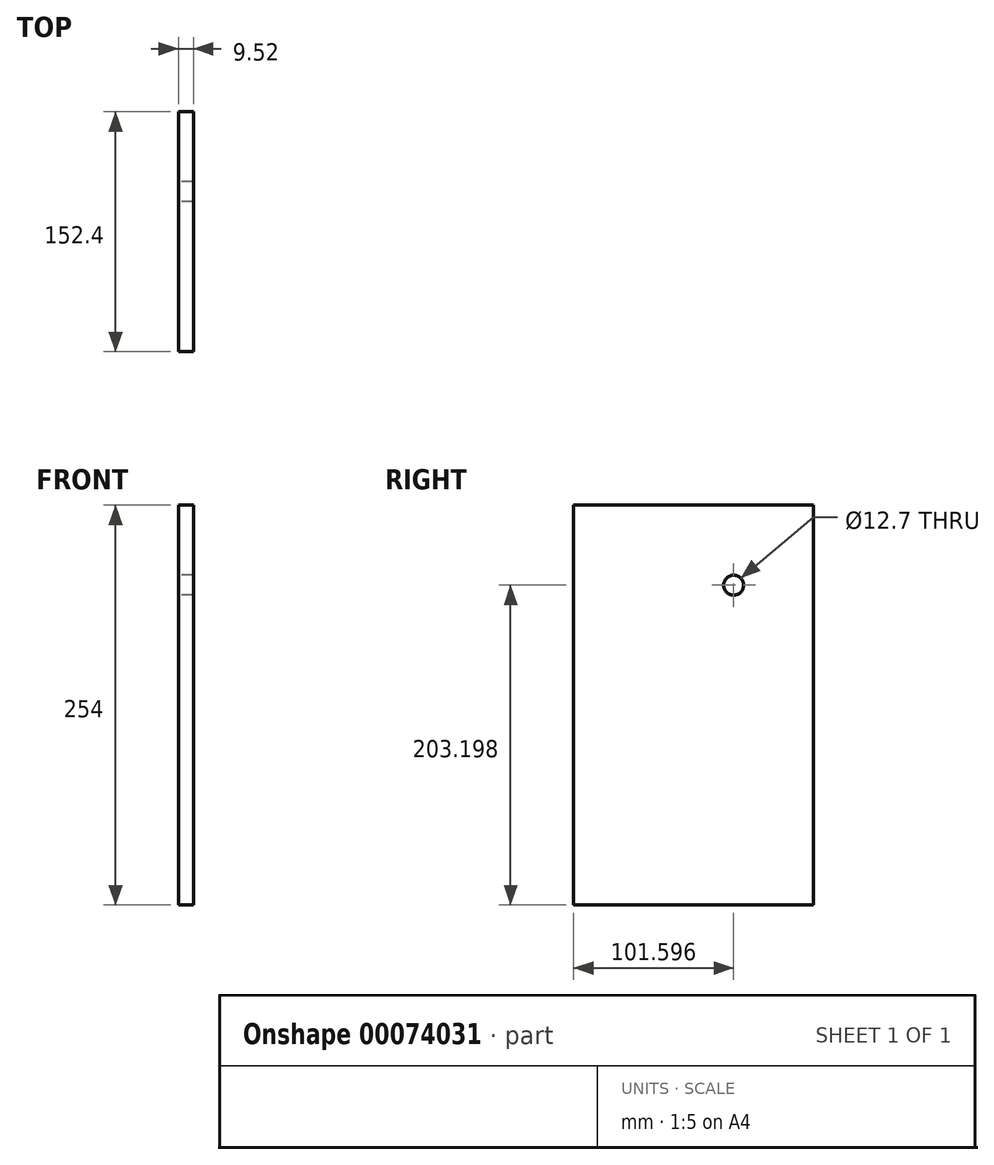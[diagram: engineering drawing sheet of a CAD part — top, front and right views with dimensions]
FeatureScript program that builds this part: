
annotation { "Feature Type Name" : "Feature", "Feature Type Description" : "" }
export const myFeature = defineFeature(function(context is Context, id is Id, definition is map)
    precondition{}
    {
        {
            var Q0;
            Q0=qCreatedBy(makeId("Right.planeOp"),FACE);
            var sketch = newSketch(context, id + "F0", { "sketchPlane" : qUnion([Q0])});
            skLineSegment(sketch, "E0.bottom", {"start": v(-96.53, 165.43) * mm, "end": v(55.87, 165.43) * mm});
            skLineSegment(sketch, "E0.top", {"start": v(-96.53, -88.57) * mm, "end": v(55.87, -88.57) * mm});
            skLineSegment(sketch, "E0.left", {"start": v(-96.53, 165.43) * mm, "end": v(-96.53, -88.57) * mm});
            skLineSegment(sketch, "E0.right", {"start": v(55.87, 165.43) * mm, "end": v(55.87, -88.57) * mm});
            skCircle(sketch, "E1", {"center": v(5.07, 114.63) * mm, "radius": 6.35 * mm});
            skSolve(sketch);
        }
        {
            var Q0;
            Q0=makeQuery(id+"F0.imprint","IMPRINT",FACE,{"disambiguationData":[TD([[makeQuery(id+"F0.imprint","IMPRINT",EDGE,{"derivedFrom":sQuery(id+"F0.wireOp",EDGE,"E0.bottom")}),-1.0]])]});
            extrude(context, id + "F1", {"entities" : qUnion([Q0]), "depth" : 9.52 * mm, "symmetric" : true});
        }
    });
